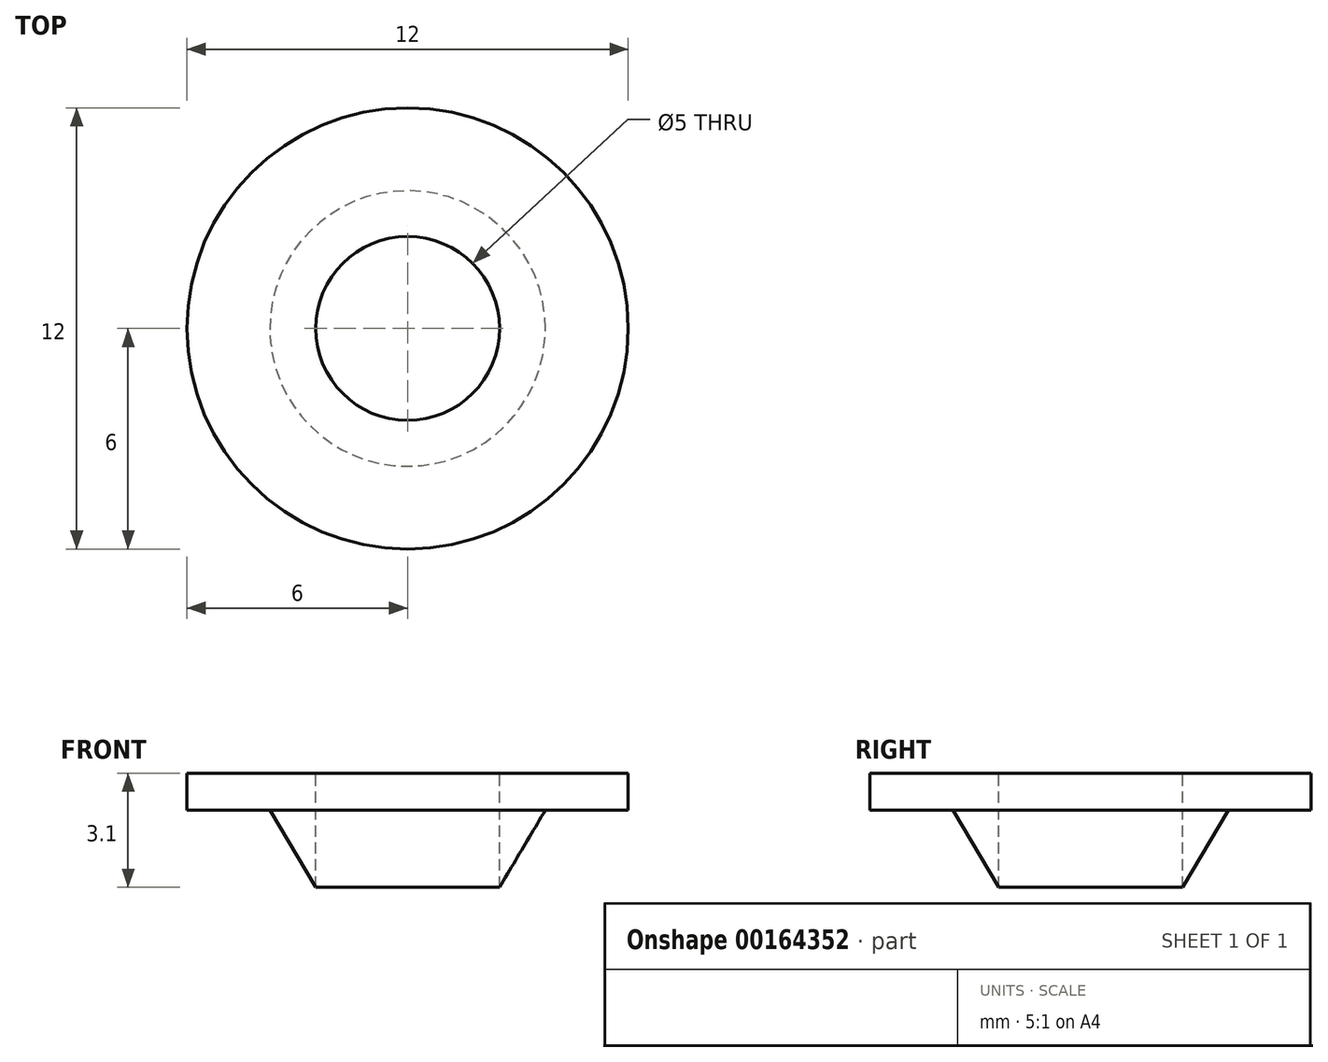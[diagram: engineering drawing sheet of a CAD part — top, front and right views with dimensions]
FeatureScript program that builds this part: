
annotation { "Feature Type Name" : "Feature", "Feature Type Description" : "" }
export const myFeature = defineFeature(function(context is Context, id is Id, definition is map)
    precondition{}
    {
        {
            var Q0;
            Q0=qCreatedBy(makeId("Front.planeOp"),FACE);
            var sketch = newSketch(context, id + "F0", { "sketchPlane" : qUnion([Q0])});
            skLineSegment(sketch, "E0", {"start": v(0, 6.77) * mm, "end": v(0, -2.47) * mm, "construction": true});
            skLineSegment(sketch, "E1", {"start": v(2.5, 0) * mm, "end": v(2.5, 3.1) * mm});
            skLineSegment(sketch, "E2", {"start": v(2.5, 3.1) * mm, "end": v(6, 3.1) * mm});
            skLineSegment(sketch, "E3", {"start": v(6, 3.1) * mm, "end": v(6, 2.1) * mm});
            skLineSegment(sketch, "E4", {"start": v(6, 2.1) * mm, "end": v(3.75, 2.1) * mm});
            skLineSegment(sketch, "E5", {"start": v(3.75, 2.1) * mm, "end": v(2.5, 0) * mm});
            skSolve(sketch);
        }
        {
            var Q0;
            Q0 = qSketchRegion(id + "F0", true);
            var Q1;
            Q1=sQuery(id+"F0.wireOp",EDGE,"E0");
            revolve(context, id + "F1", {"entities" : qUnion([Q0]), "axis" : qUnion([Q1]), "revolveType" : RevolveType.FULL});
        }
    });
